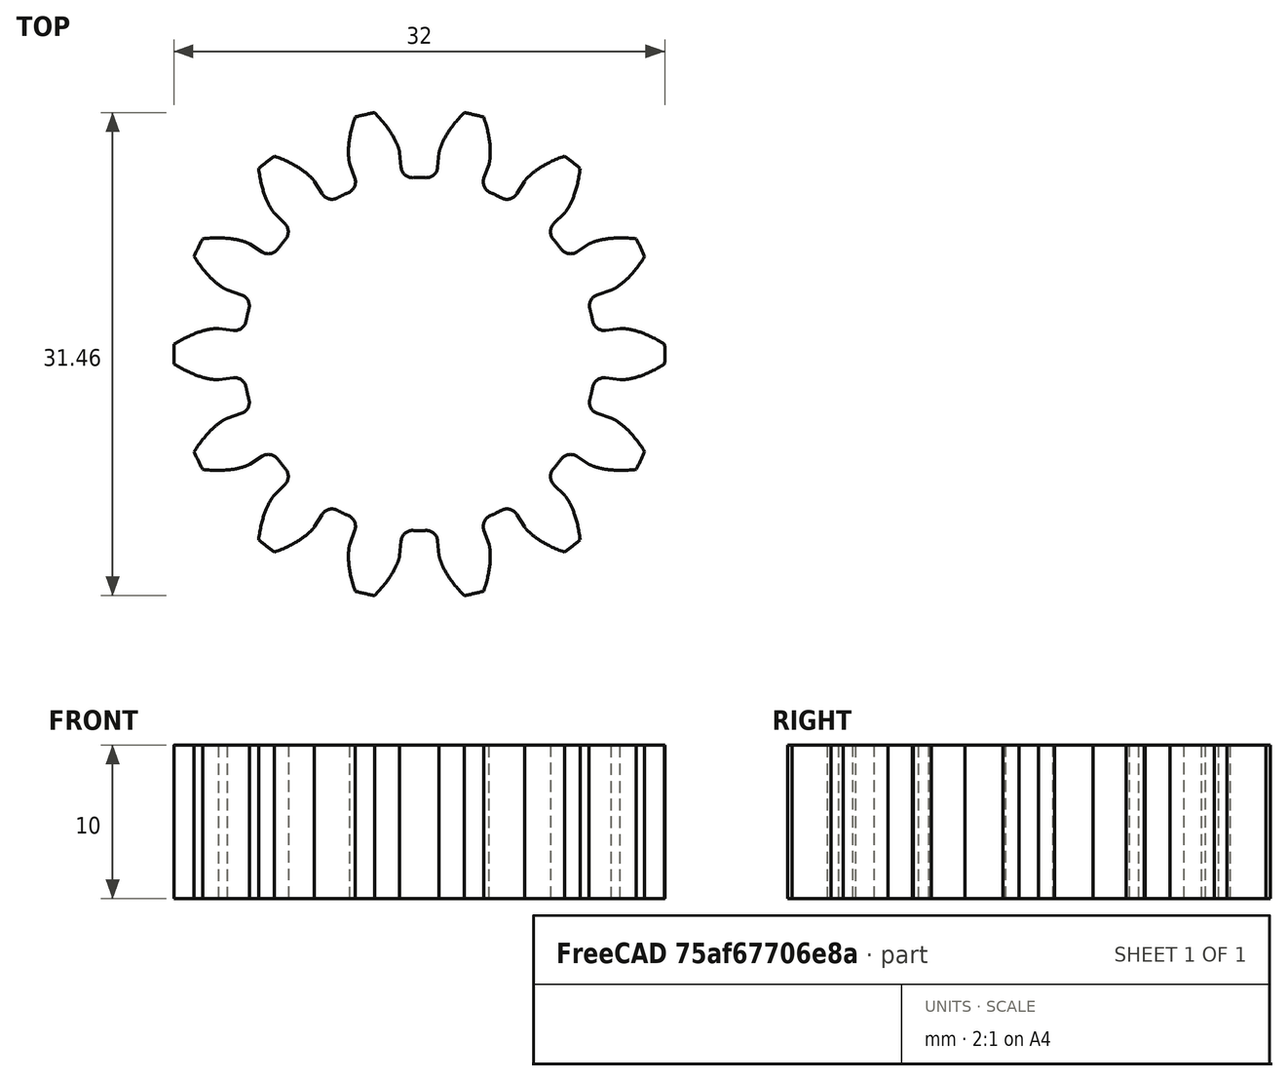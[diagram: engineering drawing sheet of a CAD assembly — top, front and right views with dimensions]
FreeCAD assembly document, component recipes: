
FREECAD ASSEMBLY — COMPONENT RECIPES ("assambly_gears_1")

This assembly document has 3 components, labeled P0..P2 below (a component is one placed body or linked part). 2 of them carry a construction recipe — the FreeCAD feature program that regenerates the part from scratch, quoted from this document or its linked companion documents; the rest are supplied as boundary geometry only. No exploded tour is included for this assembly.
COMPONENT P0 — geometry summary ("Assembly"; no construction recipe available for this part):
  bounding box: 134.0 x 134.0 x 20.0 mm
  tessellated surface: 28,656 triangles
  volume: 213219210651450264622257611185725810068079830028068023509805261430616210033398507984609615090831851520 mm^3 (59384505335175918386167428945145493309422227522824654540182619139569121575131330087154836905656320% of its bounding box)
  symmetry: 2-fold rotationally symmetric about the z axis; mirror-symmetric across its x mid-plane, y mid-plane
COMPONENT P1 — recipe-attached ("Body_14t_pd", modeled in this document).
Construction recipe (the document's own serialized feature program — sketch geometry with constraints, then the solid features built on it; lengths are millimeters unless a unit is written):

FEATURE [PartDesign::FeatureBase] BaseFeature
FEATURE [PartDesign::CoordinateSystem] LCS_g_14t
  AttacherType = Attacher::AttachEngine3D
  MapMode = 45
  Placement = pos=(1.2e-15,-4.5e-15,10) rot=(0,0,1;0rad)
  Support = -> [BaseFeature]
FEATURE [PartDesign::Body] Body  label="Body_14t_pd"
  Group = -> [BaseFeature,LCS_g_14t]
  Origin = -> Origin001
  Tip = -> BaseFeature
COMPONENT P2 — recipe-attached ("Body_in_gear", modeled in this document).
Construction recipe (the document's own serialized feature program — sketch geometry with constraints, then the solid features built on it; lengths are millimeters unless a unit is written):

FEATURE [Part::Part2DObjectPython] InvoluteGear  # Draft 2D object (typed FeaturePython)
  ExternalGear = true
  HighPrecision = true
  Modules = 2
  NumberOfTeeth = 60
  PressureAngle = 20
FEATURE [PartDesign::FeatureBase] BaseFeature001
  BaseFeature = -> Cut
FEATURE [PartDesign::CoordinateSystem] LCS_in_gear
  AttacherType = Attacher::AttachEngine3D
  MapMode = 11
  Placement = pos=(0,0,0) rot=(0,0,1;1.5708rad)
  Support = -> [BaseFeature001]
FEATURE [PartDesign::Body] Body001  label="Body_in_gear"
  BaseFeature = -> Cut
  Group = -> [BaseFeature001,InvoluteGear,LCS_in_gear]
  Origin = -> Origin002
  Tip = -> BaseFeature001
PROVENANCE & LICENSES
A FreeCAD (.FCStd) document from a public repository crawl; recipes are the document's own serialized feature recipes (and, for linked parts, companion documents' recipes).
License: as declared in the source repository (recorded in the dataset sidecar).
